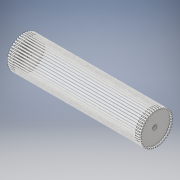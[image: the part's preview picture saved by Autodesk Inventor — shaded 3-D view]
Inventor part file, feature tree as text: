
AUTODESK INVENTOR PART (.ipt)
format: ipt  version: 2019 (Build 230136000, 136)  size: 373,760 bytes
history: native  units: in
note: dims shown in document units (in); Inventor stores cm internally (conversion verified against a paired STEP export)
features: extrude x4, sketch x4, plane x1, pattern_circular x1
ambient origin geometry x8: Origin, YZ Plane, XZ Plane, XY Plane, X Axis, Y Axis, Z Axis, Center Point
bodies: Solid1 (feature_tree)
feature tree (10):
  extrude  "Extrusion1"  Depth=0.1969in TaperAngle=0.0deg
  plane  "Work Plane1"
  extrude  "Extrusion2"  Depth=0.1969in TaperAngle=0.0deg
  extrude  "Extrusion3"  Depth=7.874in TaperAngle=0.0deg
  extrude  "Extrusion4"  Depth=6.5945in TaperAngle=0.0deg
  pattern_circular  "Circular Pattern1"  Count=45 Angle=360.0deg
  sketch  "Sketch1"  dims[d0=1.5748in d1=0.1969in d2=0.0in]
  sketch  "Sketch2"  dims[d3=6.1024in d4=0.1969in d5=0.0in]
  sketch  "Sketch3"  dims[d6=0.2165in d7=7.874in d8=0.0in]
  sketch  "Sketch4"  dims[d9=0.0591in d10=6.5945in d11=0.0984in d12=0.0in d13=0.0in d14=17.7165in d15=360.0deg]
